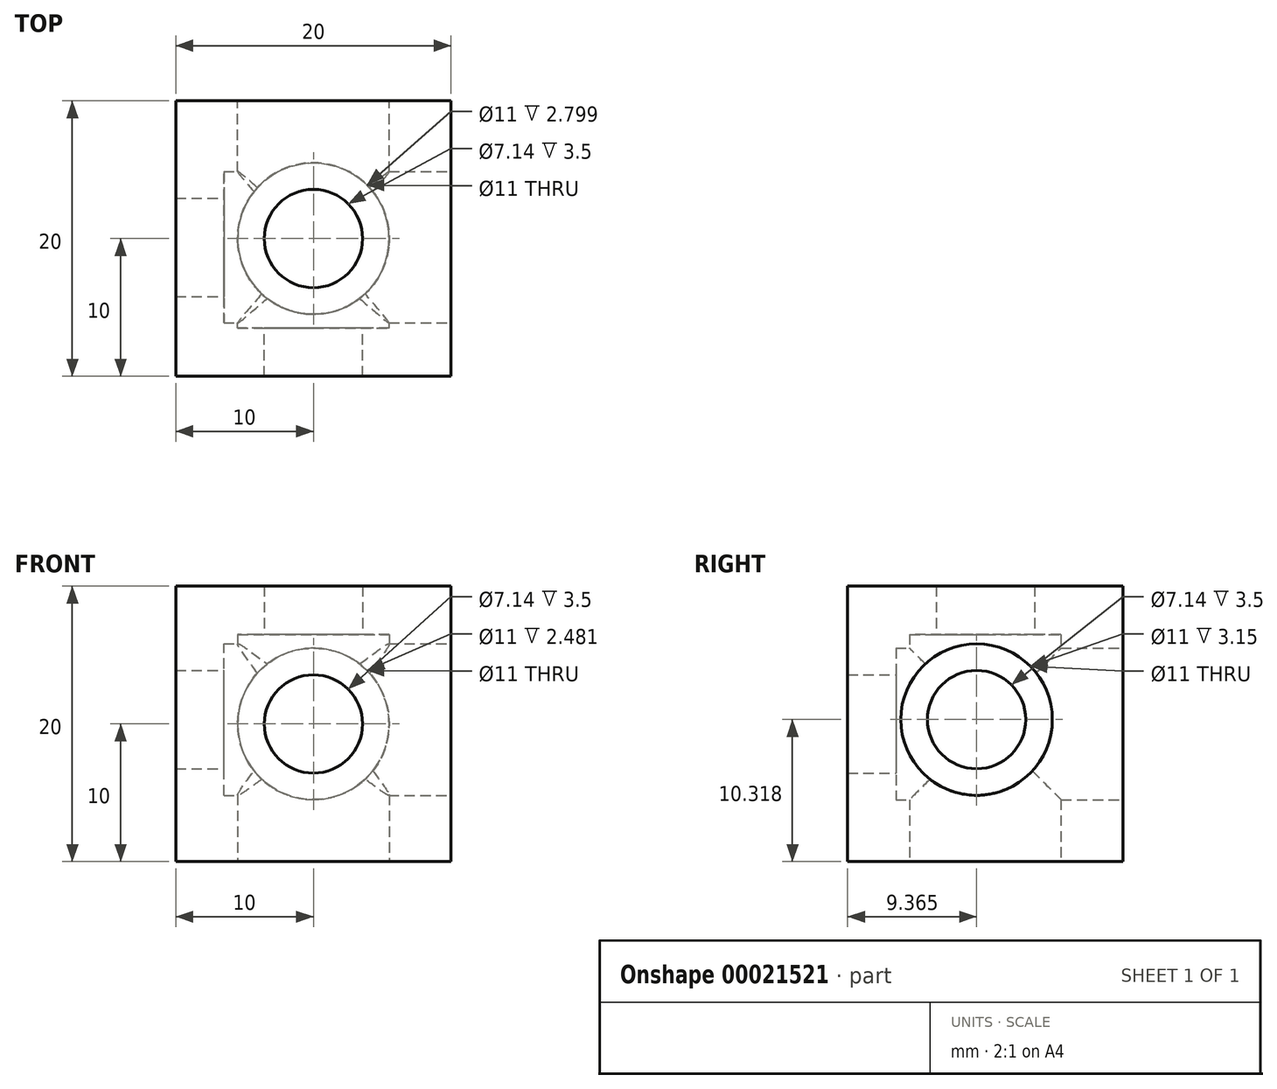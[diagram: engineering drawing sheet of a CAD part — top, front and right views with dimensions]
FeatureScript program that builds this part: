
annotation { "Feature Type Name" : "Feature", "Feature Type Description" : "" }
export const myFeature = defineFeature(function(context is Context, id is Id, definition is map)
    precondition{}
    {
        {
            var Q0;
            Q0=qCreatedBy(makeId("Top.planeOp"),FACE);
            var sketch = newSketch(context, id + "F0", { "sketchPlane" : qUnion([Q0])});
            skLineSegment(sketch, "E0.rect.bottom", {"start": v(10, 10) * mm, "end": v(-10, 10) * mm});
            skLineSegment(sketch, "E0.rect.top", {"start": v(10, -10) * mm, "end": v(-10, -10) * mm});
            skLineSegment(sketch, "E0.rect.left", {"start": v(10, 10) * mm, "end": v(10, -10) * mm});
            skLineSegment(sketch, "E0.rect.right", {"start": v(-10, 10) * mm, "end": v(-10, -10) * mm});
            skPoint(sketch, "E0.rect.middle", {"position": v(0, 0) * mm});
            skCircle(sketch, "E1", {"center": v(0, 0) * mm, "radius": 3.57 * mm});
            skCircle(sketch, "E2", {"center": v(0, 0) * mm, "radius": 5.5 * mm});
            skSolve(sketch);
        }
        {
            var Q0;
            Q0=makeQuery(id+"F0.imprint","IMPRINT",FACE,{"disambiguationData":[TD([[makeQuery(id+"F0.imprint","IMPRINT",EDGE,{"derivedFrom":sQuery(id+"F0.wireOp",EDGE,"E0.rect.bottom")}),1.0]])]});
            var Q1;
            Q1=makeQuery(id+"F0.imprint","IMPRINT",FACE,{"disambiguationData":[TD([[makeQuery(id+"F0.imprint","IMPRINT",EDGE,{"derivedFrom":sQuery(id+"F0.wireOp",EDGE,"E1")}),-1.0]])]});
            extrude(context, id + "F1", {"entities" : qUnion([Q0, Q1]), "depth" : 20 * mm});
        }
        {
            var Q0;
            Q0=makeQuery(id+"F0.imprint","IMPRINT",FACE,{"disambiguationData":[TD([[makeQuery(id+"F0.imprint","IMPRINT",EDGE,{"derivedFrom":sQuery(id+"F0.wireOp",EDGE,"E1")}),-1.0]])]});
            extrude(context, id + "F2", {"entities" : qUnion([Q0]), "operationType" : NewBodyOperationType.REMOVE, "depth" : 16.5 * mm});
        }
        {
            var Q0;
            Q0=makeQuery(id+"F1.opExtrude","SWEPT_FACE",FACE,{"disambiguationData":[OSD([sQuery(id+"F0.wireOp",EDGE,"E0.rect.bottom")])]});
            var sketch = newSketch(context, id + "F3", { "sketchPlane" : qUnion([Q0])});
            skLineSegment(sketch, "E3.rect.bottom", {"start": v(10, 20) * mm, "end": v(-10, 20) * mm});
            skLineSegment(sketch, "E3.rect.top", {"start": v(10, 0) * mm, "end": v(-10, 0) * mm});
            skLineSegment(sketch, "E3.rect.left", {"start": v(10, 20) * mm, "end": v(10, 0) * mm});
            skLineSegment(sketch, "E3.rect.right", {"start": v(-10, 20) * mm, "end": v(-10, 0) * mm});
            skPoint(sketch, "E3.rect.middle", {"position": v(0, 10) * mm});
            skCircle(sketch, "E4", {"center": v(0, 10) * mm, "radius": 3.57 * mm});
            skCircle(sketch, "E5", {"center": v(0, 10) * mm, "radius": 5.5 * mm});
            skSolve(sketch);
        }
        {
            var Q0;
            Q0=makeQuery(id+"F3.imprint","IMPRINT",FACE,{"disambiguationData":[TD([[makeQuery(id+"F3.imprint","IMPRINT",EDGE,{"derivedFrom":sQuery(id+"F3.wireOp",EDGE,"E4")}),1.0]])]});
            extrude(context, id + "F4", {"entities" : qUnion([Q0]), "operationType" : NewBodyOperationType.REMOVE, "oppositeDirection" : true, "depth" : 20 * mm});
        }
        {
            var Q0;
            Q0=makeQuery(id+"F3.imprint","IMPRINT",FACE,{"disambiguationData":[TD([[makeQuery(id+"F3.imprint","IMPRINT",EDGE,{"derivedFrom":sQuery(id+"F3.wireOp",EDGE,"E4")}),-1.0]])]});
            extrude(context, id + "F5", {"entities" : qUnion([Q0]), "operationType" : NewBodyOperationType.REMOVE, "oppositeDirection" : true, "depth" : 16.5 * mm});
        }
        {
            var Q0;
            Q0=makeQuery(id+"F1.opExtrude","SWEPT_FACE",FACE,{"disambiguationData":[OSD([sQuery(id+"F0.wireOp",EDGE,"E0.rect.left")])]});
            var sketch = newSketch(context, id + "F6", { "sketchPlane" : qUnion([Q0])});
            skLineSegment(sketch, "E6.rect.bottom", {"start": v(9.36, 20.32) * mm, "end": v(-10.64, 20.32) * mm});
            skLineSegment(sketch, "E6.rect.top", {"start": v(9.36, 0.32) * mm, "end": v(-10.64, 0.32) * mm});
            skLineSegment(sketch, "E6.rect.left", {"start": v(9.36, 20.32) * mm, "end": v(9.36, 0.32) * mm});
            skLineSegment(sketch, "E6.rect.right", {"start": v(-10.64, 20.32) * mm, "end": v(-10.64, 0.32) * mm});
            skPoint(sketch, "E6.rect.middle", {"position": v(-0.64, 10.32) * mm});
            skCircle(sketch, "E7", {"center": v(-0.64, 10.32) * mm, "radius": 3.57 * mm});
            skCircle(sketch, "E8", {"center": v(-0.64, 10.32) * mm, "radius": 5.5 * mm});
            skSolve(sketch);
        }
        {
            var Q0;
            Q0=makeQuery(id+"F6.imprint","IMPRINT",FACE,{"disambiguationData":[TD([[makeQuery(id+"F6.imprint","IMPRINT",EDGE,{"derivedFrom":sQuery(id+"F6.wireOp",EDGE,"E7")}),1.0]])]});
            extrude(context, id + "F7", {"entities" : qUnion([Q0]), "operationType" : NewBodyOperationType.REMOVE, "oppositeDirection" : true, "depth" : 20 * mm});
        }
        {
            var Q0;
            Q0=makeQuery(id+"F6.imprint","IMPRINT",FACE,{"disambiguationData":[TD([[makeQuery(id+"F6.imprint","IMPRINT",EDGE,{"derivedFrom":sQuery(id+"F6.wireOp",EDGE,"E7")}),-1.0]])]});
            extrude(context, id + "F8", {"entities" : qUnion([Q0]), "operationType" : NewBodyOperationType.REMOVE, "oppositeDirection" : true, "depth" : 16.5 * mm});
        }
    });
